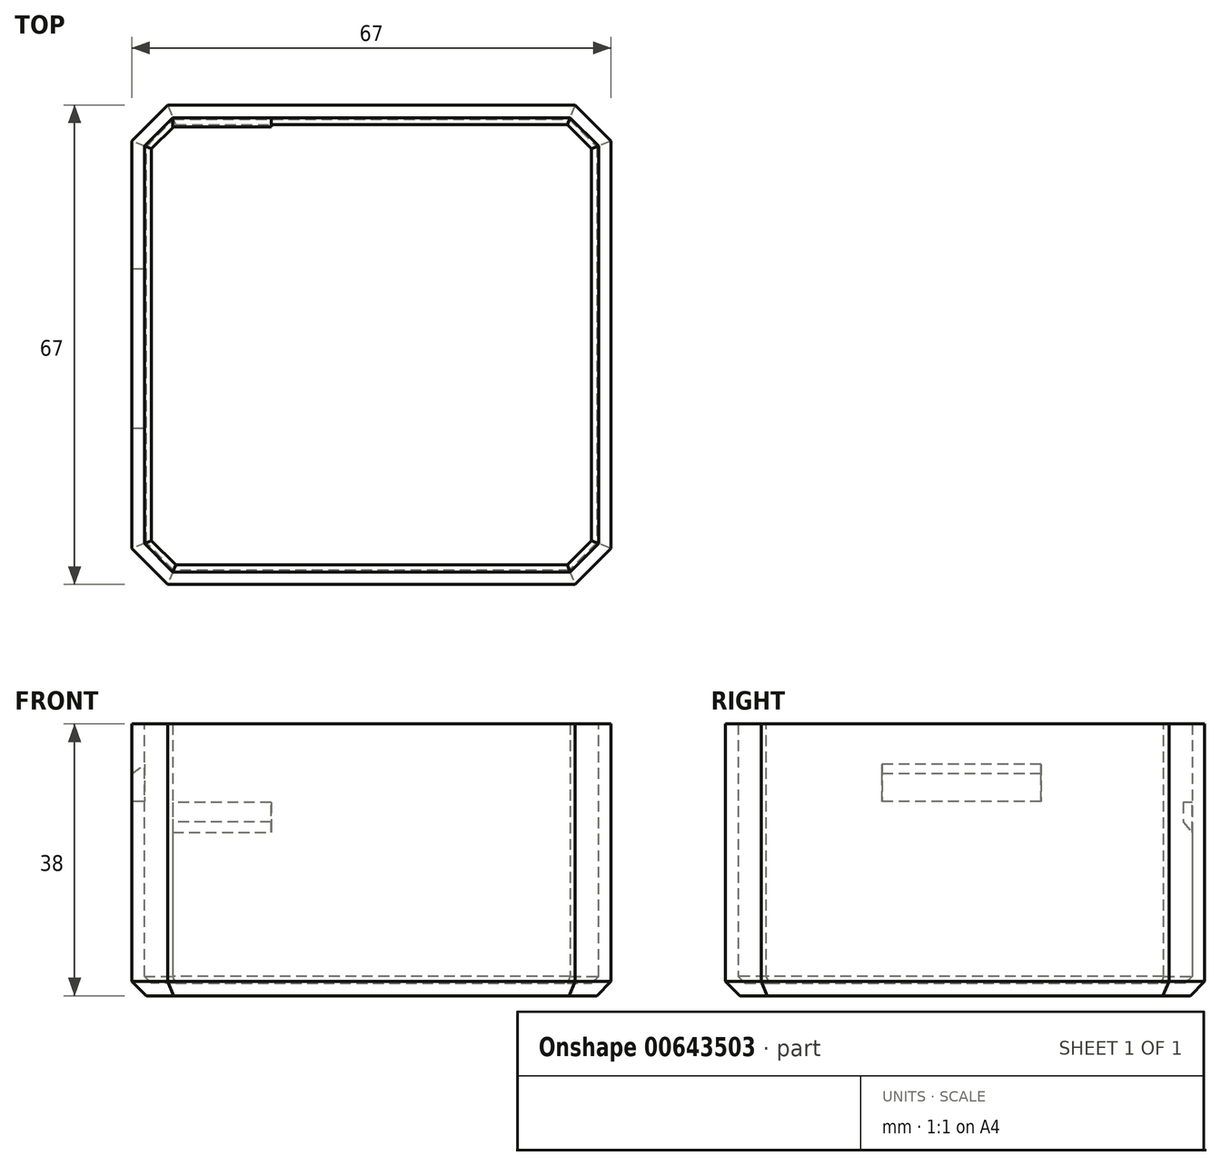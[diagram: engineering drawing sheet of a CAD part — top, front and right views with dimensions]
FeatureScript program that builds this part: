
annotation { "Feature Type Name" : "Feature", "Feature Type Description" : "" }
export const myFeature = defineFeature(function(context is Context, id is Id, definition is map)
    precondition{}
    {
        {
            var Q0;
            Q0=qCreatedBy(makeId("Top.planeOp"),FACE);
            var sketch = newSketch(context, id + "F0", { "sketchPlane" : qUnion([Q0])});
            skLineSegment(sketch, "E0.bottom", {"start": v(0, 0) * mm, "end": v(67, 0) * mm});
            skLineSegment(sketch, "E0.top", {"start": v(0, 67) * mm, "end": v(67, 67) * mm});
            skLineSegment(sketch, "E0.left", {"start": v(0, 0) * mm, "end": v(0, 67) * mm});
            skLineSegment(sketch, "E0.right", {"start": v(67, 0) * mm, "end": v(67, 67) * mm});
            skSolve(sketch);
        }
        {
            var Q0;
            Q0=makeQuery(id+"F0.imprint","IMPRINT",FACE,{"disambiguationData":[TD([[makeQuery(id+"F0.imprint","IMPRINT",EDGE,{"derivedFrom":sQuery(id+"F0.wireOp",EDGE,"E0.bottom")}),1.0]])]});
            extrude(context, id + "F1", {"entities" : qUnion([Q0]), "depth" : 38 * mm, "offsetDistance" : 25 * mm});
        }
        {
            var Q0;
            Q0=makeQuery(id+"F1.opExtrude","SWEPT_EDGE",EDGE,{"disambiguationData":[OSD([sQuery(id+"F0.wireOp",EDGE,"E0.top"),sQuery(id+"F0.wireOp",EDGE,"E0.right")])]});
            var Q1;
            Q1=makeQuery(id+"F1.opExtrude","SWEPT_EDGE",EDGE,{"disambiguationData":[OSD([sQuery(id+"F0.wireOp",EDGE,"E0.bottom"),sQuery(id+"F0.wireOp",EDGE,"E0.right")])]});
            var Q2;
            Q2=makeQuery(id+"F1.opExtrude","SWEPT_EDGE",EDGE,{"disambiguationData":[OSD([sQuery(id+"F0.wireOp",EDGE,"E0.bottom"),sQuery(id+"F0.wireOp",EDGE,"E0.left")])]});
            var Q3;
            Q3=makeQuery(id+"F1.opExtrude","SWEPT_EDGE",EDGE,{"disambiguationData":[OSD([sQuery(id+"F0.wireOp",EDGE,"E0.top"),sQuery(id+"F0.wireOp",EDGE,"E0.left")])]});
            chamfer(context, id + "F2", {"entities" : qUnion([Q0, Q1, Q2, Q3]), "width" : 5 * mm, "tangentPropagation" : true});
        }
        {
            var Q0;
            Q0=makeQuery(id+"F1.opExtrude","CAP_EDGE",EDGE,{"disambiguationData":[OSD([sQuery(id+"F0.wireOp",EDGE,"E0.left")])],"isStart":true});
            var Q1;
            Q1=makeQuery(id+"F1.opExtrude","CAP_EDGE",EDGE,{"disambiguationData":[OSD([sQuery(id+"F0.wireOp",EDGE,"E0.bottom")])],"isStart":true});
            var Q2;
            {var subQ0=sQuery(id+"F0.wireOp",EDGE,"E0.left");var subQ1=sQuery(id+"F0.wireOp",EDGE,"E0.bottom");Q2=makeQuery(id+"F2.opChamfer","BLEND_EDGE",EDGE,{"blendedFrom":[makeQuery(id+"F1.opExtrude","SWEPT_EDGE",EDGE,{"disambiguationData":[OSD([subQ1,subQ0])]}),makeQuery(id+"F1.opExtrude","CAP_FACE",FACE,{"disambiguationData":[OSD([subQ1,sQuery(id+"F0.wireOp",EDGE,"E0.top"),subQ0,sQuery(id+"F0.wireOp",EDGE,"E0.right")])],"isStart":true})],"blendedInto":[makeQuery(id+"F1.opExtrude","CAP_FACE",FACE,{"disambiguationData":[OSD([subQ1,sQuery(id+"F0.wireOp",EDGE,"E0.top"),subQ0,sQuery(id+"F0.wireOp",EDGE,"E0.right")])],"isStart":true})]});}
            var Q3;
            {var subQ0=sQuery(id+"F0.wireOp",EDGE,"E0.right");var subQ1=sQuery(id+"F0.wireOp",EDGE,"E0.bottom");Q3=makeQuery(id+"F2.opChamfer","BLEND_EDGE",EDGE,{"blendedFrom":[makeQuery(id+"F1.opExtrude","SWEPT_EDGE",EDGE,{"disambiguationData":[OSD([subQ1,subQ0])]}),makeQuery(id+"F1.opExtrude","CAP_FACE",FACE,{"disambiguationData":[OSD([subQ1,sQuery(id+"F0.wireOp",EDGE,"E0.top"),sQuery(id+"F0.wireOp",EDGE,"E0.left"),subQ0])],"isStart":true})],"blendedInto":[makeQuery(id+"F1.opExtrude","CAP_FACE",FACE,{"disambiguationData":[OSD([subQ1,sQuery(id+"F0.wireOp",EDGE,"E0.top"),sQuery(id+"F0.wireOp",EDGE,"E0.left"),subQ0])],"isStart":true})]});}
            var Q4;
            Q4=makeQuery(id+"F1.opExtrude","CAP_FACE",FACE,{"disambiguationData":[OSD([sQuery(id+"F0.wireOp",EDGE,"E0.bottom"),sQuery(id+"F0.wireOp",EDGE,"E0.top"),sQuery(id+"F0.wireOp",EDGE,"E0.left"),sQuery(id+"F0.wireOp",EDGE,"E0.right")])],"isStart":true});
            chamfer(context, id + "F3", {"entities" : qUnion([Q0, Q1, Q2, Q3, Q4]), "width" : 2 * mm, "tangentPropagation" : true});
        }
        {
            var Q0;
            Q0=makeQuery(id+"F1.opExtrude","CAP_FACE",FACE,{"disambiguationData":[OSD([sQuery(id+"F0.wireOp",EDGE,"E0.bottom"),sQuery(id+"F0.wireOp",EDGE,"E0.top"),sQuery(id+"F0.wireOp",EDGE,"E0.left"),sQuery(id+"F0.wireOp",EDGE,"E0.right")])],"isStart":false});
            shell(context, id + "F4", {"entities" : qUnion([Q0]), "thickness" : 1.75 * mm});
        }
        {
            var Q0;
            Q0=qCreatedBy(makeId("Front.planeOp"),FACE);
            cPlane(context, id + "F5", {"entities" : qUnion([Q0]), "cplaneType" : CPlaneType.OFFSET, "offset" : 21.87 * mm, "oppositeDirection" : true, "width" : 150 * mm, "height" : 150 * mm});
        }
        {
            var Q0;
            Q0=qCreatedBy(id+"F5.planeOp",FACE);
            var sketch = newSketch(context, id + "F6", { "sketchPlane" : qUnion([Q0])});
            skLineSegment(sketch, "E1", {"start": v(0, 31) * mm, "end": v(1.75, 32.36) * mm});
            skLineSegment(sketch, "E2", {"start": v(1.75, 32.36) * mm, "end": v(1.75, 27.14) * mm});
            skLineSegment(sketch, "E3", {"start": v(1.75, 27.14) * mm, "end": v(0, 27.14) * mm});
            skLineSegment(sketch, "E4", {"start": v(0, 27.14) * mm, "end": v(0, 31) * mm});
            skSolve(sketch);
        }
        {
            var Q0;
            Q0=qSketchRegion(id+"F6",true);
            extrude(context, id + "F7", {"entities" : qUnion([Q0]), "operationType" : NewBodyOperationType.REMOVE, "oppositeDirection" : true, "depth" : 22.26 * mm, "offsetDistance" : 25 * mm});
        }
        {
            var Q0;
            Q0=makeQuery(id+"F1.opExtrude","SWEPT_FACE",FACE,{"disambiguationData":[OSD([sQuery(id+"F0.wireOp",EDGE,"E0.left")])]});
            var Q1;
            Q1=makeQuery(id+"F1.opExtrude","SWEPT_FACE",FACE,{"disambiguationData":[OSD([sQuery(id+"F0.wireOp",EDGE,"E0.right")])]});
            cPlane(context, id + "F8", {"entities" : qUnion([Q0, Q1]), "cplaneType" : CPlaneType.MID_PLANE, "offset" : 25 * mm, "width" : 150 * mm, "height" : 150 * mm});
        }
        {
            var Q0;
            {var subQ0=sQuery(id+"F0.wireOp",EDGE,"E0.top");var subQ1=sQuery(id+"F0.wireOp",EDGE,"E0.left");Q0=makeQuery(id+"F4.opShell","OFFSET_EDGE",EDGE,{"disambiguationData":[OSD([subQ0,subQ1]),TDD([makeQuery(id+"F2.opChamfer","BLEND_EDGE",EDGE,{"blendedFrom":[makeQuery(id+"F1.opExtrude","SWEPT_EDGE",EDGE,{"disambiguationData":[OSD([subQ0,subQ1])]}),makeQuery(id+"F1.opExtrude","SWEPT_FACE",FACE,{"disambiguationData":[OSD([subQ0])]})],"blendedInto":[makeQuery(id+"F1.opExtrude","SWEPT_FACE",FACE,{"disambiguationData":[OSD([subQ0])]})]})])]});}
            cPlane(context, id + "F9", {"entities" : qUnion([Q0]), "cplaneType" : CPlaneType.LINE_ANGLE, "offset" : 25 * mm, "angle" : 0 * degree, "width" : 150 * mm, "height" : 150 * mm});
        }
        {
            var Q0;
            Q0=qCreatedBy(id+"F9.planeOp",FACE);
            var sketch = newSketch(context, id + "F10", { "sketchPlane" : qUnion([Q0])});
            skLineSegment(sketch, "E5", {"start": v(-65.97, 27) * mm, "end": v(-63.97, 27) * mm});
            skLineSegment(sketch, "E6", {"start": v(-63.97, 27) * mm, "end": v(-63.97, 24.3) * mm});
            skLineSegment(sketch, "E7", {"start": v(-63.97, 24.3) * mm, "end": v(-65.97, 22) * mm});
            skLineSegment(sketch, "E8", {"start": v(-65.97, 22) * mm, "end": v(-65.97, 27) * mm});
            skSolve(sketch);
        }
        {
            var Q0;
            Q0=makeQuery(id+"F10.imprint","IMPRINT",FACE,{"disambiguationData":[TD([[makeQuery(id+"F10.imprint","IMPRINT",EDGE,{"derivedFrom":sQuery(id+"F10.wireOp",EDGE,"E5")}),-1.0]])]});
            extrude(context, id + "F11", {"entities" : qUnion([Q0]), "operationType" : NewBodyOperationType.ADD, "oppositeDirection" : true, "depth" : 13.75 * mm, "offsetDistance" : 25 * mm});
        }
        {
            var Q0;
            Q0=makeQuery(id+"F1.opExtrude","SWEPT_FACE",FACE,{"disambiguationData":[OSD([sQuery(id+"F0.wireOp",EDGE,"E0.bottom")])]});
            var Q1;
            Q1=makeQuery(id+"F1.opExtrude","SWEPT_FACE",FACE,{"disambiguationData":[OSD([sQuery(id+"F0.wireOp",EDGE,"E0.top")])]});
            cPlane(context, id + "F12", {"entities" : qUnion([Q0, Q1]), "cplaneType" : CPlaneType.MID_PLANE, "offset" : 25 * mm, "width" : 150 * mm, "height" : 150 * mm});
        }
    });
